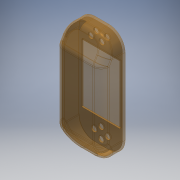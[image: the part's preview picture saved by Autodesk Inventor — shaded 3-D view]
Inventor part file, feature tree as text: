
AUTODESK INVENTOR PART (.ipt)
format: ipt  version: 2016 SP1 (Build 200210100, 210)  size: 311,808 bytes
history: native  units: mm
features: extrude x3, sketch x3, chamfer x2, fillet x2, shell x1
ambient origin geometry x8: Origin, YZ Plane, XZ Plane, XY Plane, X Axis, Y Axis, Z Axis, Center Point
bodies: Solide1 (feature_tree)
feature tree (11):
  extrude  "Extrusion1"  Depth=200.0mm
  chamfer  "Chanfrein1"  Distance=85.0mm
  chamfer  "Chanfrein2"  Distance=42.5mm
  fillet  "Congé3"  Radius=100.0mm
  fillet  "Congé4"  Radius=42.0mm
  shell  "Coque1"  Thickness=20.0mm
  extrude  "Extrusion2"  Depth=20.0mm TaperAngle=60.0deg
  extrude  "Extrusion3"  Depth=30.0mm
  sketch  "Esquisse1"
  sketch  "Esquisse3"
  sketch  "Esquisse4"
